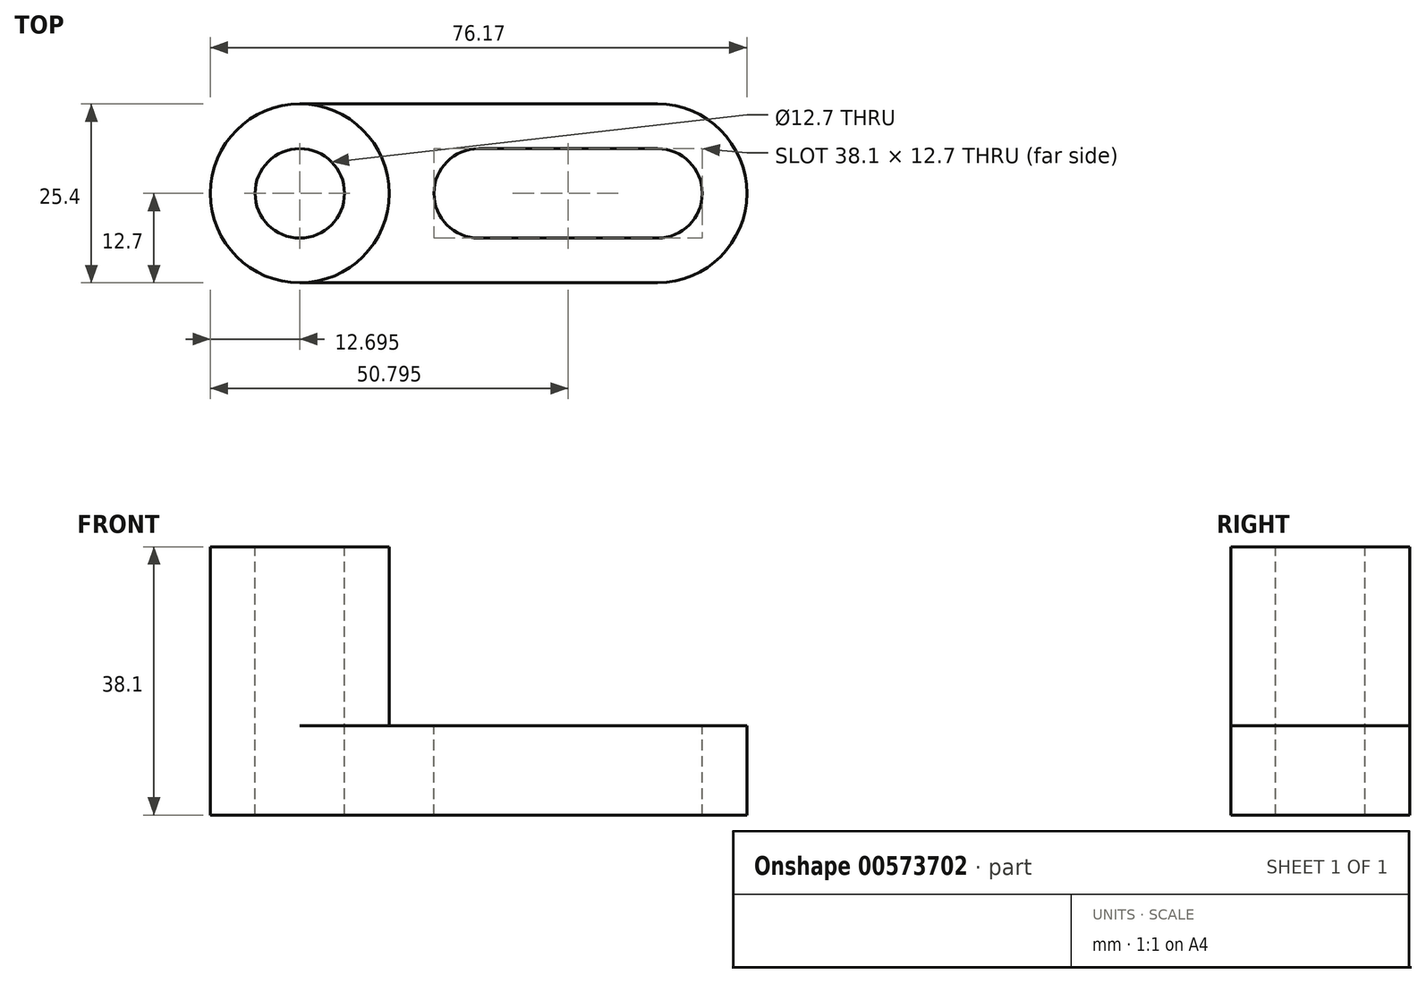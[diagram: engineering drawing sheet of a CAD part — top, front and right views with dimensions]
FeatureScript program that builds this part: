
annotation { "Feature Type Name" : "Feature", "Feature Type Description" : "" }
export const myFeature = defineFeature(function(context is Context, id is Id, definition is map)
    precondition{}
    {
        {
            var Q0;
            Q0=qCreatedBy(makeId("Front.planeOp"),FACE);
            var sketch = newSketch(context, id + "F0", { "sketchPlane" : qUnion([Q0])});
            skLineSegment(sketch, "E0", {"start": v(-74.18, 42.78) * mm, "end": v(-74.18, 8.4) * mm});
            skLineSegment(sketch, "E1", {"start": v(-74.18, 8.4) * mm, "end": v(2.02, 8.4) * mm});
            skLineSegment(sketch, "E2", {"start": v(2.02, 8.4) * mm, "end": v(2.02, 21.1) * mm});
            skLineSegment(sketch, "E3", {"start": v(2.02, 21.1) * mm, "end": v(-48.78, 21.1) * mm});
            skLineSegment(sketch, "E4", {"start": v(-48.78, 21.1) * mm, "end": v(-48.78, 46.5) * mm});
            skLineSegment(sketch, "E5", {"start": v(-48.78, 46.5) * mm, "end": v(-74.18, 46.5) * mm});
            skLineSegment(sketch, "E6", {"start": v(-74.18, 46.5) * mm, "end": v(-74.18, 42.78) * mm});
            skSolve(sketch);
        }
        {
            var Q0;
            Q0=makeQuery(id+"F0.imprint","IMPRINT",FACE,{"disambiguationData":[TD([[makeQuery(id+"F0.imprint","IMPRINT",EDGE,{"derivedFrom":sQuery(id+"F0.wireOp",EDGE,"E0")}),1.0]])]});
            extrude(context, id + "F1", {"entities" : qUnion([Q0]), "depth" : 25.4 * mm, "offsetDistance" : 25.4 * mm});
        }
        {
            var Q0;
            Q0=makeQuery(id+"F1.opExtrude","SWEPT_FACE",FACE,{"disambiguationData":[OSD([sQuery(id+"F0.wireOp",EDGE,"E5")])]});
            var sketch = newSketch(context, id + "F2", { "sketchPlane" : qUnion([Q0])});
            skCircle(sketch, "E7", {"center": v(-61.48, -12.7) * mm, "radius": 12.7 * mm});
            skCircle(sketch, "E8", {"center": v(-61.48, -12.7) * mm, "radius": 6.35 * mm});
            skSolve(sketch);
        }
        {
            var Q0;
            {var subQ0=sQuery(id+"F2.wireOp",EDGE,"E7");var subQ1=sQuery(id+"F0.wireOp",EDGE,"E5");var subQ2=makeQuery(id+"F1.opExtrude","CAP_EDGE",EDGE,{"disambiguationData":[OSD([subQ1])],"isStart":true});var subQ3=makeQuery(id+"F2.imprint","INTERSECT",VERTEX,{"derivedFrom":[subQ2,subQ0]});Q0=makeQuery(id+"F2.imprint","IMPRINT",FACE,{"disambiguationData":[TD([[makeQuery(id+"F2.imprint","IMPRINT",EDGE,{"disambiguationData":[TD([[subQ3,-1.0]])],"derivedFrom":subQ0}),-1.0]])]});}
            var Q1;
            {var subQ0=sQuery(id+"F2.wireOp",EDGE,"E7");var subQ1=sQuery(id+"F0.wireOp",EDGE,"E5");var subQ4=makeQuery(id+"F1.opExtrude","CAP_EDGE",EDGE,{"disambiguationData":[OSD([subQ1])],"isStart":false});var subQ5=makeQuery(id+"F2.imprint","INTERSECT",VERTEX,{"derivedFrom":[subQ4,subQ0]});Q1=makeQuery(id+"F2.imprint","IMPRINT",FACE,{"disambiguationData":[TD([[makeQuery(id+"F2.imprint","IMPRINT",EDGE,{"disambiguationData":[TD([[subQ5,1.0]])],"derivedFrom":subQ0}),-1.0]])]});}
            var Q2;
            Q2=makeQuery(id+"F2.imprint","IMPRINT",FACE,{"disambiguationData":[TD([[makeQuery(id+"F2.imprint","IMPRINT",EDGE,{"derivedFrom":sQuery(id+"F2.wireOp",EDGE,"E8")}),1.0]])]});
            extrude(context, id + "F3", {"entities" : qUnion([Q0, Q1, Q2]), "operationType" : NewBodyOperationType.REMOVE, "endBound" : BoundingType.THROUGH_ALL, "oppositeDirection" : true, "depth" : 25.4 * mm, "offsetDistance" : 25.4 * mm});
        }
        {
            var Q0;
            Q0=makeQuery(id+"F1.opExtrude","SWEPT_FACE",FACE,{"disambiguationData":[OSD([sQuery(id+"F0.wireOp",EDGE,"E5")])]});
            var sketch = newSketch(context, id + "F4", { "sketchPlane" : qUnion([Q0])});
            skCircle(sketch, "E9", {"center": v(-61.48, -12.7) * mm, "radius": 12.7 * mm});
            skSolve(sketch);
        }
        {
            var Q0;
            {var subQ1=sQuery(id+"F0.wireOp",EDGE,"E5");var subQ2=makeQuery(id+"F1.opExtrude","CAP_EDGE",EDGE,{"disambiguationData":[OSD([subQ1])],"isStart":true});Q0=makeQuery(id+"F4.imprint","IMPRINT",FACE,{"disambiguationData":[TD([[makeQuery(id+"F4.imprint","IMPRINT",EDGE,{"derivedFrom":subQ2}),1.0]])]});}
            var Q1;
            {var subQ1=sQuery(id+"F0.wireOp",EDGE,"E5");var subQ2=makeQuery(id+"F1.opExtrude","CAP_EDGE",EDGE,{"disambiguationData":[OSD([subQ1])],"isStart":false});Q1=makeQuery(id+"F4.imprint","IMPRINT",FACE,{"disambiguationData":[TD([[makeQuery(id+"F4.imprint","IMPRINT",EDGE,{"derivedFrom":subQ2}),-1.0]])]});}
            extrude(context, id + "F5", {"entities" : qUnion([Q0, Q1]), "operationType" : NewBodyOperationType.REMOVE, "oppositeDirection" : true, "depth" : 25.4 * mm, "offsetDistance" : 25.4 * mm});
        }
        {
            var Q0;
            {var subQ0=sQuery(id+"F0.wireOp",EDGE,"E5");var subQ1=makeQuery(id+"F1.opExtrude","CAP_EDGE",EDGE,{"disambiguationData":[OSD([subQ0])],"isStart":false});var subQ2=sQuery(id+"F0.wireOp",EDGE,"E4");var subQ3=makeQuery(id+"F1.opExtrude","SWEPT_EDGE",EDGE,{"disambiguationData":[OSD([subQ2,subQ0])]});var subQ4=sQuery(id+"F4.wireOp",EDGE,"E9");var subQ6=makeQuery(id+"F1.opExtrude","CAP_EDGE",EDGE,{"disambiguationData":[OSD([subQ0])],"isStart":true});Q0=makeQuery(id+"F5.boolean.opBoolean","MERGE",FACE,{"derivedFrom":[makeQuery(id+"F1.opExtrude","SWEPT_FACE",FACE,{"disambiguationData":[OSD([sQuery(id+"F0.wireOp",EDGE,"E3")])]}),makeQuery(id+"F5.opExtrude","CAP_FACE",FACE,{"disambiguationData":[OSD([subQ2,subQ0,subQ4]),TDD([makeQuery(id+"F4.imprint","IMPRINT",EDGE,{"disambiguationData":[TD([[makeQuery(id+"F4.imprint","INTERSECT",VERTEX,{"derivedFrom":[subQ6,subQ4]}),1.0]])],"derivedFrom":subQ4}),makeQuery(id+"F4.imprint","IMPRINT",EDGE,{"derivedFrom":subQ6}),makeQuery(id+"F4.imprint","IMPRINT",EDGE,{"disambiguationData":[TD([[makeQuery(id+"F4.imprint","INTERSECT",VERTEX,{"derivedFrom":[subQ3,subQ6]}),1.0]])],"derivedFrom":subQ3})])],"isStart":false}),makeQuery(id+"F5.opExtrude","CAP_FACE",FACE,{"disambiguationData":[OSD([subQ2,subQ0,subQ4]),TDD([makeQuery(id+"F4.imprint","IMPRINT",EDGE,{"disambiguationData":[TD([[makeQuery(id+"F4.imprint","INTERSECT",VERTEX,{"derivedFrom":[subQ1,subQ4]}),-1.0]])],"derivedFrom":subQ4}),makeQuery(id+"F4.imprint","IMPRINT",EDGE,{"derivedFrom":subQ1}),makeQuery(id+"F4.imprint","IMPRINT",EDGE,{"disambiguationData":[TD([[makeQuery(id+"F4.imprint","INTERSECT",VERTEX,{"derivedFrom":[subQ3,subQ1]}),-1.0]])],"derivedFrom":subQ3})])],"isStart":false})]});}
            var sketch = newSketch(context, id + "F6", { "sketchPlane" : qUnion([Q0])});
            skCircle(sketch, "E10", {"center": v(-36.08, -12.7) * mm, "radius": 6.35 * mm});
            skCircle(sketch, "E11", {"center": v(-10.68, -12.7) * mm, "radius": 6.35 * mm});
            skLineSegment(sketch, "E12", {"start": v(-36.08, -6.35) * mm, "end": v(-10.68, -6.35) * mm});
            skLineSegment(sketch, "E13", {"start": v(-10.68, -19.05) * mm, "end": v(-36.08, -19.05) * mm});
            skSolve(sketch);
        }
        {
            var Q0;
            {var subQ0=sQuery(id+"F6.wireOp",EDGE,"E11");var subQ1=makeQuery(id+"F6.imprint","INTERSECT",VERTEX,{"derivedFrom":[subQ0,sQuery(id+"F6.wireOp",EDGE,"E12")]});Q0=makeQuery(id+"F6.imprint","IMPRINT",FACE,{"disambiguationData":[TD([[makeQuery(id+"F6.imprint","IMPRINT",EDGE,{"disambiguationData":[TD([[subQ1,-1.0]])],"derivedFrom":subQ0}),1.0]])]});}
            var sketch = newSketch(context, id + "F7", { "sketchPlane" : qUnion([Q0])});
            skArc(sketch, "E14", {"start": v(-10.47, -25.4) * mm, "mid": v(1.95, -12.58) * mm, "end": v(-10.7, 0) * mm});
            skSolve(sketch);
        }
        {
            var Q0;
            {var subQ0=sQuery(id+"F6.wireOp",EDGE,"E10");var subQ1=makeQuery(id+"F6.imprint","INTERSECT",VERTEX,{"derivedFrom":[subQ0,sQuery(id+"F6.wireOp",EDGE,"E12")]});Q0=makeQuery(id+"F6.imprint","IMPRINT",FACE,{"disambiguationData":[TD([[makeQuery(id+"F6.imprint","IMPRINT",EDGE,{"disambiguationData":[TD([[subQ1,-1.0]])],"derivedFrom":subQ0}),1.0]])]});}
            var Q1;
            {var subQ0=sQuery(id+"F6.wireOp",EDGE,"E12");Q1=makeQuery(id+"F6.imprint","IMPRINT",FACE,{"disambiguationData":[TD([[makeQuery(id+"F6.imprint","IMPRINT",EDGE,{"derivedFrom":subQ0}),-1.0]])]});}
            var Q2;
            {var subQ0=sQuery(id+"F6.wireOp",EDGE,"E11");var subQ1=makeQuery(id+"F6.imprint","INTERSECT",VERTEX,{"derivedFrom":[subQ0,sQuery(id+"F6.wireOp",EDGE,"E12")]});Q2=makeQuery(id+"F6.imprint","IMPRINT",FACE,{"disambiguationData":[TD([[makeQuery(id+"F6.imprint","IMPRINT",EDGE,{"disambiguationData":[TD([[subQ1,-1.0]])],"derivedFrom":subQ0}),1.0]])]});}
            extrude(context, id + "F8", {"entities" : qUnion([Q0, Q1, Q2]), "operationType" : NewBodyOperationType.REMOVE, "endBound" : BoundingType.THROUGH_ALL, "oppositeDirection" : true, "depth" : 25.4 * mm, "offsetDistance" : 25.4 * mm});
        }
        {
            var Q0;
            {var subQ0=sQuery(id+"F6.wireOp",EDGE,"E11");var subQ1=makeQuery(id+"F6.imprint","INTERSECT",VERTEX,{"derivedFrom":[subQ0,sQuery(id+"F6.wireOp",EDGE,"E12")]});Q0=makeQuery(id+"F7.imprint","IMPRINT",FACE,{"disambiguationData":[TD([[makeQuery(id+"F7.imprint","IMPRINT",EDGE,{"derivedFrom":makeQuery(id+"F6.imprint","IMPRINT",EDGE,{"disambiguationData":[TD([[subQ1,-1.0]])],"derivedFrom":subQ0})}),1.0]])]});}
            extrude(context, id + "F9", {"entities" : qUnion([Q0]), "operationType" : NewBodyOperationType.REMOVE, "endBound" : BoundingType.THROUGH_ALL, "oppositeDirection" : true, "depth" : 25.4 * mm, "offsetDistance" : 25.4 * mm});
        }
        {
            var Q0;
            {var subQ0=sQuery(id+"F0.wireOp",EDGE,"E5");var subQ1=makeQuery(id+"F1.opExtrude","CAP_EDGE",EDGE,{"disambiguationData":[OSD([subQ0])],"isStart":false});var subQ2=sQuery(id+"F0.wireOp",EDGE,"E4");var subQ3=makeQuery(id+"F1.opExtrude","SWEPT_EDGE",EDGE,{"disambiguationData":[OSD([subQ2,subQ0])]});var subQ4=sQuery(id+"F4.wireOp",EDGE,"E9");var subQ6=makeQuery(id+"F1.opExtrude","CAP_EDGE",EDGE,{"disambiguationData":[OSD([subQ0])],"isStart":true});Q0=makeQuery(id+"F5.boolean.opBoolean","MERGE",FACE,{"derivedFrom":[makeQuery(id+"F1.opExtrude","SWEPT_FACE",FACE,{"disambiguationData":[OSD([sQuery(id+"F0.wireOp",EDGE,"E3")])]}),makeQuery(id+"F5.opExtrude","CAP_FACE",FACE,{"disambiguationData":[OSD([subQ2,subQ0,subQ4]),TDD([makeQuery(id+"F4.imprint","IMPRINT",EDGE,{"disambiguationData":[TD([[makeQuery(id+"F4.imprint","INTERSECT",VERTEX,{"derivedFrom":[subQ6,subQ4]}),1.0]])],"derivedFrom":subQ4}),makeQuery(id+"F4.imprint","IMPRINT",EDGE,{"derivedFrom":subQ6}),makeQuery(id+"F4.imprint","IMPRINT",EDGE,{"disambiguationData":[TD([[makeQuery(id+"F4.imprint","INTERSECT",VERTEX,{"derivedFrom":[subQ3,subQ6]}),1.0]])],"derivedFrom":subQ3})])],"isStart":false}),makeQuery(id+"F5.opExtrude","CAP_FACE",FACE,{"disambiguationData":[OSD([subQ2,subQ0,subQ4]),TDD([makeQuery(id+"F4.imprint","IMPRINT",EDGE,{"disambiguationData":[TD([[makeQuery(id+"F4.imprint","INTERSECT",VERTEX,{"derivedFrom":[subQ1,subQ4]}),-1.0]])],"derivedFrom":subQ4}),makeQuery(id+"F4.imprint","IMPRINT",EDGE,{"derivedFrom":subQ1}),makeQuery(id+"F4.imprint","IMPRINT",EDGE,{"disambiguationData":[TD([[makeQuery(id+"F4.imprint","INTERSECT",VERTEX,{"derivedFrom":[subQ3,subQ1]}),-1.0]])],"derivedFrom":subQ3})])],"isStart":false})]});}
            var sketch = newSketch(context, id + "F10", { "sketchPlane" : qUnion([Q0])});
            skArc(sketch, "E15", {"start": v(-10.68, -25.4) * mm, "mid": v(1.99, -12.7) * mm, "end": v(-10.68, 0) * mm});
            skSolve(sketch);
        }
        {
            var Q0;
            {var subQ0=sQuery(id+"F10.wireOp",EDGE,"E15");Q0=makeQuery(id+"F10.imprint","IMPRINT",FACE,{"disambiguationData":[TD([[makeQuery(id+"F10.imprint","IMPRINT",EDGE,{"derivedFrom":subQ0}),-1.0]])]});}
            extrude(context, id + "F11", {"entities" : qUnion([Q0]), "operationType" : NewBodyOperationType.ADD, "endBound" : BoundingType.THROUGH_ALL, "depth" : 25.4 * mm, "offsetDistance" : 25.4 * mm});
        }
        {
            var Q0;
            Q0=makeQuery(id+"F11.opExtrude","CAP_FACE",FACE,{"disambiguationData":[OSD([sQuery(id+"F0.wireOp",EDGE,"E2"),sQuery(id+"F0.wireOp",EDGE,"E3"),sQuery(id+"F0.wireOp",EDGE,"E5"),sQuery(id+"F10.wireOp",EDGE,"E15")])],"isStart":false});
            extrude(context, id + "F12", {"entities" : qUnion([Q0]), "operationType" : NewBodyOperationType.REMOVE, "endBound" : BoundingType.THROUGH_ALL, "oppositeDirection" : true, "depth" : 25.4 * mm, "offsetDistance" : 25.4 * mm});
        }
    });
